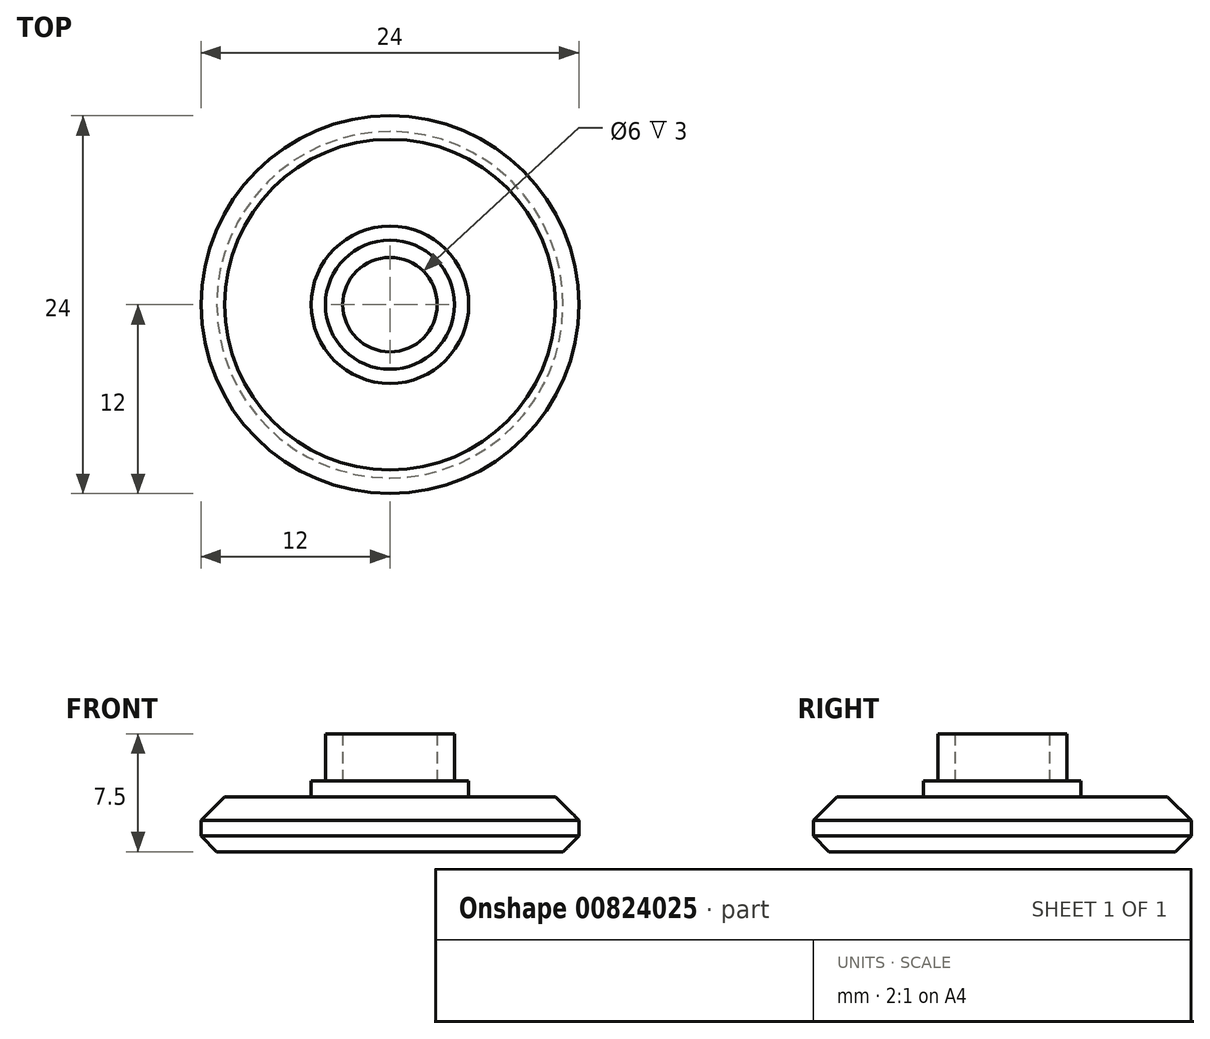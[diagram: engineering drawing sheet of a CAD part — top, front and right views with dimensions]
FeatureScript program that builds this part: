
annotation { "Feature Type Name" : "Feature", "Feature Type Description" : "" }
export const myFeature = defineFeature(function(context is Context, id is Id, definition is map)
    precondition{}
    {
        {
            var Q0;
            Q0=qCreatedBy(makeId("Top.planeOp"),FACE);
            var sketch = newSketch(context, id + "F0", { "sketchPlane" : qUnion([Q0])});
            skCircle(sketch, "E0", {"center": v(0, 0) * mm, "radius": 12 * mm});
            skCircle(sketch, "E1", {"center": v(0, 0) * mm, "radius": 11 * mm});
            skCircle(sketch, "E2", {"center": v(0, 0) * mm, "radius": 4.1 * mm});
            skCircle(sketch, "E3", {"center": v(0, 0) * mm, "radius": 3 * mm});
            skCircle(sketch, "E4", {"center": v(0, 0) * mm, "radius": 5 * mm});
            skSolve(sketch);
        }
        {
            var Q0;
            Q0=makeQuery(id+"F0.imprint","IMPRINT",FACE,{"disambiguationData":[TD([[makeQuery(id+"F0.imprint","IMPRINT",EDGE,{"derivedFrom":sQuery(id+"F0.wireOp",EDGE,"E0")}),1.0]])]});
            var Q1;
            Q1=makeQuery(id+"F0.imprint","IMPRINT",FACE,{"disambiguationData":[TD([[makeQuery(id+"F0.imprint","IMPRINT",EDGE,{"derivedFrom":sQuery(id+"F0.wireOp",EDGE,"E1")}),1.0]])]});
            var Q2;
            Q2=makeQuery(id+"F0.imprint","IMPRINT",FACE,{"disambiguationData":[TD([[makeQuery(id+"F0.imprint","IMPRINT",EDGE,{"derivedFrom":sQuery(id+"F0.wireOp",EDGE,"E3")}),1.0]])]});
            var Q3;
            Q3=makeQuery(id+"F0.imprint","IMPRINT",FACE,{"disambiguationData":[TD([[makeQuery(id+"F0.imprint","IMPRINT",EDGE,{"derivedFrom":sQuery(id+"F0.wireOp",EDGE,"E2")}),1.0]])]});
            var Q4;
            Q4=makeQuery(id+"F0.imprint","IMPRINT",FACE,{"disambiguationData":[TD([[makeQuery(id+"F0.imprint","IMPRINT",EDGE,{"derivedFrom":sQuery(id+"F0.wireOp",EDGE,"E2")}),-1.0]])]});
            extrude(context, id + "F1", {"entities" : qUnion([Q0, Q1, Q2, Q3, Q4]), "depth" : 2 * mm, "offsetDistance" : 25 * mm});
        }
        {
            var Q0;
            Q0=makeQuery(id+"F0.imprint","IMPRINT",FACE,{"disambiguationData":[TD([[makeQuery(id+"F0.imprint","IMPRINT",EDGE,{"derivedFrom":sQuery(id+"F0.wireOp",EDGE,"E1")}),1.0]])]});
            var Q1;
            Q1=makeQuery(id+"F0.imprint","IMPRINT",FACE,{"disambiguationData":[TD([[makeQuery(id+"F0.imprint","IMPRINT",EDGE,{"derivedFrom":sQuery(id+"F0.wireOp",EDGE,"E2")}),1.0]])]});
            var Q2;
            Q2=makeQuery(id+"F0.imprint","IMPRINT",FACE,{"disambiguationData":[TD([[makeQuery(id+"F0.imprint","IMPRINT",EDGE,{"derivedFrom":sQuery(id+"F0.wireOp",EDGE,"E3")}),1.0]])]});
            var Q3;
            Q3=makeQuery(id+"F0.imprint","IMPRINT",FACE,{"disambiguationData":[TD([[makeQuery(id+"F0.imprint","IMPRINT",EDGE,{"derivedFrom":sQuery(id+"F0.wireOp",EDGE,"E2")}),-1.0]])]});
            extrude(context, id + "F2", {"entities" : qUnion([Q0, Q1, Q2, Q3]), "operationType" : NewBodyOperationType.ADD, "depth" : 3.5 * mm, "offsetDistance" : 25 * mm});
        }
        {
            var Q0;
            Q0=makeQuery(id+"F2.boolean.opBoolean","INTERSECT",EDGE,{"derivedFrom":[makeQuery(id+"F1.opExtrude","CAP_FACE",FACE,{"disambiguationData":[OSD([sQuery(id+"F0.wireOp",EDGE,"E0")])],"isStart":false}),makeQuery(id+"F2.opExtrude","SWEPT_FACE",FACE,{"disambiguationData":[OSD([sQuery(id+"F0.wireOp",EDGE,"E1")])]})]});
            chamfer(context, id + "F3", {"entities" : qUnion([Q0]), "width" : 1 * mm, "tangentPropagation" : true});
        }
        {
            var Q0;
            Q0=makeQuery(id+"F0.imprint","IMPRINT",FACE,{"disambiguationData":[TD([[makeQuery(id+"F0.imprint","IMPRINT",EDGE,{"derivedFrom":sQuery(id+"F0.wireOp",EDGE,"E3")}),1.0]])]});
            var Q1;
            Q1=makeQuery(id+"F0.imprint","IMPRINT",FACE,{"disambiguationData":[TD([[makeQuery(id+"F0.imprint","IMPRINT",EDGE,{"derivedFrom":sQuery(id+"F0.wireOp",EDGE,"E2")}),1.0]])]});
            var Q2;
            Q2=makeQuery(id+"F0.imprint","IMPRINT",FACE,{"disambiguationData":[TD([[makeQuery(id+"F0.imprint","IMPRINT",EDGE,{"derivedFrom":sQuery(id+"F0.wireOp",EDGE,"E2")}),-1.0]])]});
            extrude(context, id + "F4", {"entities" : qUnion([Q0, Q1, Q2]), "operationType" : NewBodyOperationType.ADD, "depth" : 4.5 * mm, "offsetDistance" : 25 * mm});
        }
        {
            var Q0;
            Q0=makeQuery(id+"F0.imprint","IMPRINT",FACE,{"disambiguationData":[TD([[makeQuery(id+"F0.imprint","IMPRINT",EDGE,{"derivedFrom":sQuery(id+"F0.wireOp",EDGE,"E2")}),1.0]])]});
            extrude(context, id + "F5", {"entities" : qUnion([Q0]), "operationType" : NewBodyOperationType.ADD, "depth" : 7.5 * mm, "offsetDistance" : 25 * mm});
        }
        {
            var Q0;
            Q0=makeQuery(id+"F1.opExtrude","CAP_EDGE",EDGE,{"disambiguationData":[OSD([sQuery(id+"F0.wireOp",EDGE,"E0")])],"isStart":true});
            chamfer(context, id + "F6", {"entities" : qUnion([Q0]), "width" : 1 * mm, "tangentPropagation" : true});
        }
        {
            var Q0;
            Q0=makeQuery(id+"F2.opExtrude","CAP_EDGE",EDGE,{"disambiguationData":[OSD([sQuery(id+"F0.wireOp",EDGE,"E1")])],"isStart":false});
            chamfer(context, id + "F7", {"entities" : qUnion([Q0]), "width" : 0.5 * mm, "tangentPropagation" : true});
        }
    });
